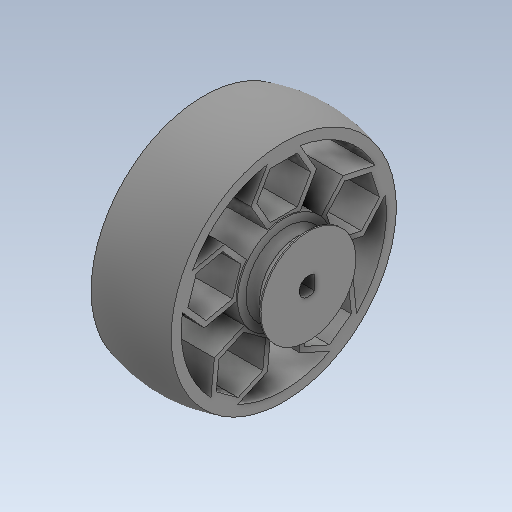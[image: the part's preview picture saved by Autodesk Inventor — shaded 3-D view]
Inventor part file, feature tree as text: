
AUTODESK INVENTOR PART (.ipt)
format: ipt  version: 2020 (Build 240168000, 168)  size: 401,920 bytes
history: native  units: in
note: dims shown in document units (in); Inventor stores cm internally (conversion verified against a paired STEP export)
features: sketch x4, extrude x2, revolve x2, projected_geometry x1
ambient origin geometry x8: Origin, YZ Plane, XZ Plane, XY Plane, X Axis, Y Axis, Z Axis, Center Point
bodies: Solid1 (feature_tree)
feature tree (9):
  extrude  "Extrusion1"  Depth=0.0394in
  sketch  "Sketch3"  dims[d6=0.6063in d7=0.1575in]
  revolve  "Revolution1"  [1 undecoded]
  extrude  "Extrusion2"  Depth=0.1575in
  revolve  "Revolution2"  [1 undecoded]
  sketch  "Sketch1"  dims[d0=0.1181in d1=0.0394in]
  sketch  "Sketch2"  dims[d3=1.437in d4=0.1181in]
  projected_geometry  "Projected Loop1"
  sketch  "Sketch4"  dims[d8=0.0in d9=1.437in d10=0.063in d11=0.0315in d16=0.5118in d17=0.0in d19=360.0deg d20=0.0787in d24=0.0394in d25=90.0deg d26=45.0deg d28=0.0079in d29=1.9685in d31=360.0deg]
note: 2 required parameter values undecoded (feature->parameter linkage not recoverable at this tier; creation-order binding heuristic only, values carry confidence <= 0.55)
